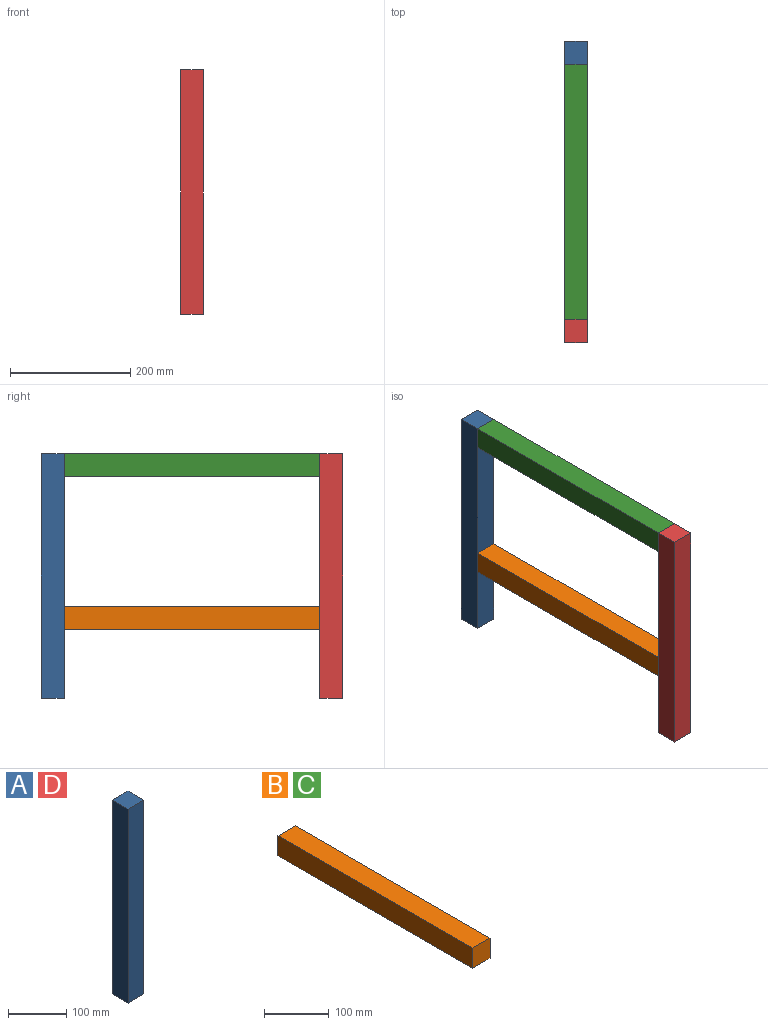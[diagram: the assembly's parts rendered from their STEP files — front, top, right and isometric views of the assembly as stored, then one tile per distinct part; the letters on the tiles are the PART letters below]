
ASSEMBLY  parts=4 mates=3
PART A: 6 faces, bbox 38x38x406 mm
  f0: plane 38x38mm, normal (0,0,1), area 1444mm2, adj f1,f3,f4,f5
  f1: plane 406x38mm, normal (-1,0,0), area 15428mm2, adj f0,f2,f4,f5
  f2: plane 38x38mm, normal (0,0,-1), area 1444mm2, adj f1,f3,f4,f5
  f3: plane 406x38mm, normal (1,0,0), area 15428mm2, adj f0,f2,f4,f5
  f4: plane 406x38mm, normal (0,-1,0), area 15428mm2, adj f0,f1,f2,f3
  f5: plane 406x38mm, normal (0,1,0), area 15428mm2, adj f0,f1,f2,f3
PART B: 6 faces, bbox 38x424x38 mm
  f0: plane 424x38mm, normal (0,0,1), area 16112mm2, adj f1,f3,f4,f5
  f1: plane 38x38mm, normal (0,-1,0), area 1444mm2, adj f0,f2,f4,f5
  f2: plane 424x38mm, normal (0,0,-1), area 16112mm2, adj f1,f3,f4,f5
  f3: plane 38x38mm, normal (0,1,0), area 1444mm2, adj f0,f2,f4,f5
  f4: plane 424x38mm, normal (1,0,0), area 16112mm2, adj f0,f1,f2,f3
  f5: plane 424x38mm, normal (-1,0,0), area 16112mm2, adj f0,f1,f2,f3
PART C: same geometry as B
PART D: same geometry as A
PLACE A t=(-259.94,493.5,-87.03)mm
PLACE B t=(-297.94,455.5,27.97)mm
PLACE C t=(-297.94,455.5,280.97)mm
PLACE D t=(-259.94,31.5,-87.03)mm
MATE fastened C.f3 <-> A.f4  axis (0,1,0) through (-278.94,455.5,318.97)mm
MATE fastened D.f5 <-> B.f1  axis (0,1,0) through (-278.94,31.5,-87.03)mm
MATE fastened C.f1 <-> D.f5  axis (0,-1,0) through (-278.94,31.5,318.97)mm
